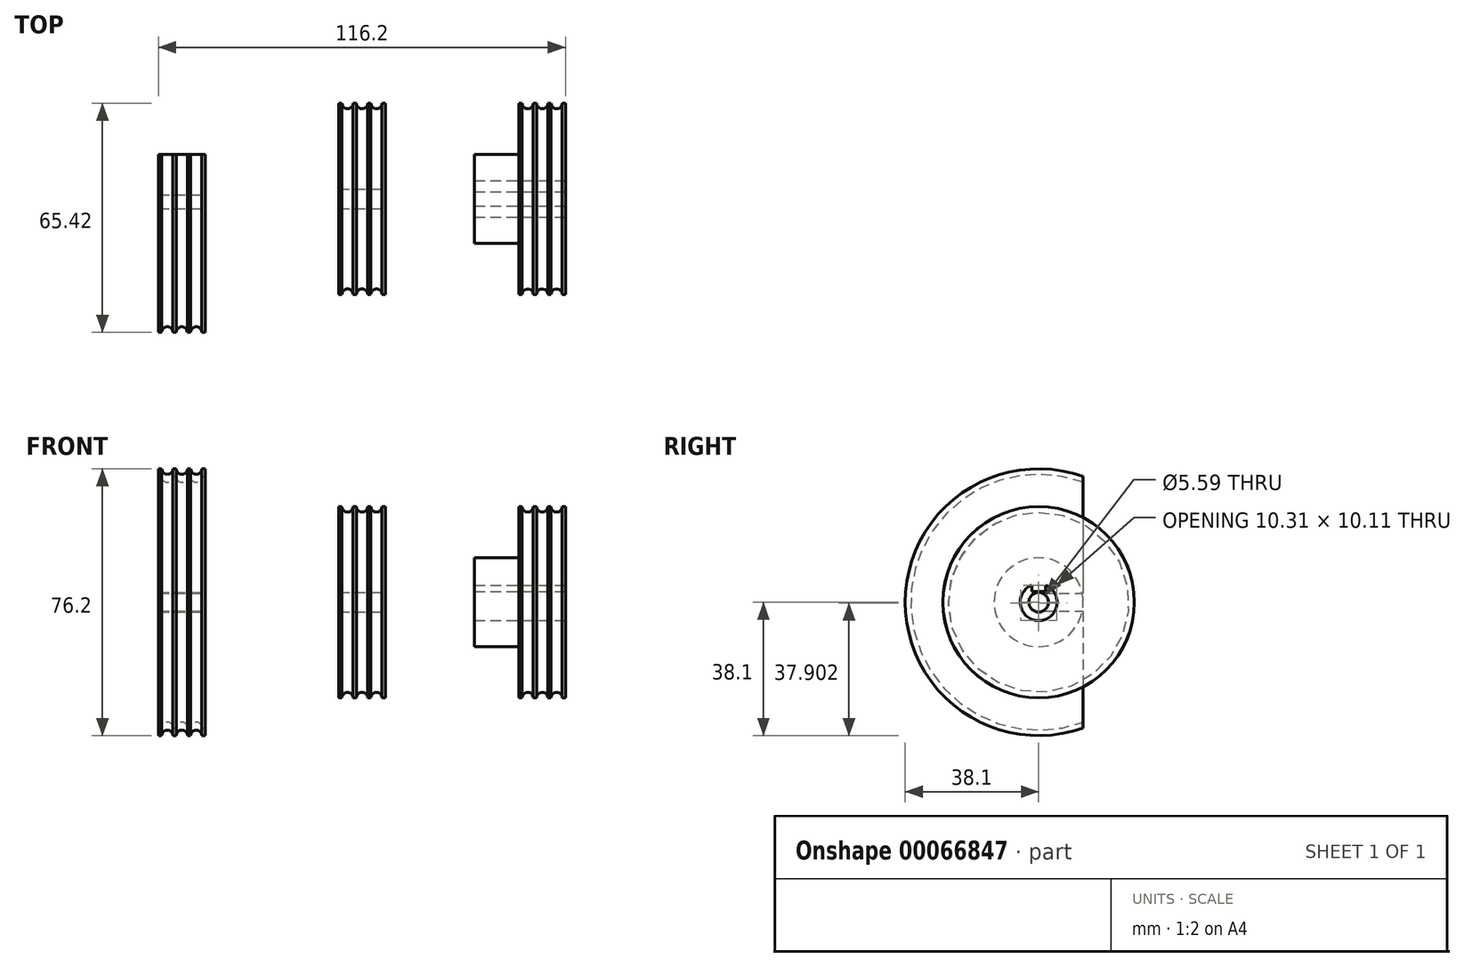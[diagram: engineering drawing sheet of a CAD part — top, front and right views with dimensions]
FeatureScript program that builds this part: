
annotation { "Feature Type Name" : "Feature", "Feature Type Description" : "" }
export const myFeature = defineFeature(function(context is Context, id is Id, definition is map)
    precondition{}
    {
        {
            var Q0;
            Q0=qCreatedBy(makeId("Front.planeOp"),FACE);
            var sketch = newSketch(context, id + "F0", { "sketchPlane" : qUnion([Q0])});
            skArc(sketch, "E0", {"start": v(-12.38, 27.32) * mm, "mid": v(-10.8, 25.72) * mm, "end": v(-9.2, 27.3) * mm});
            skArc(sketch, "E1", {"start": v(-8.25, 27.3) * mm, "mid": v(-6.67, 25.72) * mm, "end": v(-5.08, 27.3) * mm});
            skArc(sketch, "E2", {"start": v(-4.13, 27.3) * mm, "mid": v(-2.54, 25.72) * mm, "end": v(-0.95, 27.3) * mm});
            skLineSegment(sketch, "E3", {"start": v(-9.2, 27.3) * mm, "end": v(-8.25, 27.3) * mm});
            skLineSegment(sketch, "E4", {"start": v(-12.38, 27.32) * mm, "end": v(-13.33, 27.32) * mm});
            skLineSegment(sketch, "E5", {"start": v(-0.95, 27.3) * mm, "end": v(0, 27.3) * mm});
            skLineSegment(sketch, "E6", {"start": v(-5.08, 27.3) * mm, "end": v(-4.13, 27.3) * mm});
            skLineSegment(sketch, "E7", {"start": v(-13.33, 27.32) * mm, "end": v(-13.33, 0) * mm});
            skLineSegment(sketch, "E8", {"start": v(-13.33, 0) * mm, "end": v(0, 0) * mm});
            skLineSegment(sketch, "E9", {"start": v(0, 0) * mm, "end": v(0, 27.3) * mm});
            skArc(sketch, "E10", {"start": v(39.05, 27.32) * mm, "mid": v(40.63, 25.72) * mm, "end": v(42.23, 27.3) * mm});
            skArc(sketch, "E11", {"start": v(43.18, 27.3) * mm, "mid": v(44.77, 25.72) * mm, "end": v(46.35, 27.3) * mm});
            skArc(sketch, "E12", {"start": v(47.3, 27.3) * mm, "mid": v(48.9, 25.72) * mm, "end": v(50.48, 27.3) * mm});
            skLineSegment(sketch, "E13", {"start": v(42.23, 27.3) * mm, "end": v(43.18, 27.3) * mm});
            skLineSegment(sketch, "E14", {"start": v(39.05, 27.32) * mm, "end": v(38.1, 27.32) * mm});
            skLineSegment(sketch, "E15", {"start": v(50.48, 27.3) * mm, "end": v(51.43, 27.3) * mm});
            skLineSegment(sketch, "E16", {"start": v(46.35, 27.3) * mm, "end": v(47.3, 27.3) * mm});
            skLineSegment(sketch, "E17", {"start": v(38.1, 27.32) * mm, "end": v(38.1, 0) * mm});
            skLineSegment(sketch, "E18", {"start": v(38.1, 0) * mm, "end": v(51.43, 0) * mm});
            skLineSegment(sketch, "E19", {"start": v(51.43, 0) * mm, "end": v(51.43, 27.3) * mm});
            skArc(sketch, "E20", {"start": v(-59.69, 38.1) * mm, "mid": v(-58.1, 36.51) * mm, "end": v(-56.51, 38.1) * mm});
            skArc(sketch, "E21", {"start": v(-55.56, 38.1) * mm, "mid": v(-53.97, 36.51) * mm, "end": v(-52.39, 38.1) * mm});
            skLineSegment(sketch, "E22", {"start": v(-60.64, 38.1) * mm, "end": v(-59.69, 38.1) * mm});
            skLineSegment(sketch, "E23", {"start": v(-63.82, 38.1) * mm, "end": v(-64.77, 38.1) * mm});
            skLineSegment(sketch, "E24", {"start": v(-52.39, 38.1) * mm, "end": v(-51.43, 38.1) * mm});
            skLineSegment(sketch, "E25", {"start": v(-56.51, 38.1) * mm, "end": v(-55.56, 38.1) * mm});
            skLineSegment(sketch, "E26", {"start": v(-64.77, 38.1) * mm, "end": v(-64.77, 0) * mm});
            skLineSegment(sketch, "E27", {"start": v(-64.77, 0) * mm, "end": v(-51.43, 0) * mm});
            skLineSegment(sketch, "E28", {"start": v(-51.43, 0) * mm, "end": v(-51.43, 38.1) * mm});
            skArc(sketch, "E29", {"start": v(-63.82, 38.1) * mm, "mid": v(-62.23, 36.51) * mm, "end": v(-60.64, 38.1) * mm});
            skSolve(sketch);
        }
        {
            var Q0;
            Q0=makeQuery(id+"F0.imprint","IMPRINT",FACE,{"disambiguationData":[TD([[makeQuery(id+"F0.imprint","IMPRINT",EDGE,{"derivedFrom":sQuery(id+"F0.wireOp",EDGE,"E0")}),-1.0]])]});
            var Q1;
            Q1=makeQuery(id+"F0.imprint","IMPRINT",FACE,{"disambiguationData":[TD([[makeQuery(id+"F0.imprint","IMPRINT",EDGE,{"derivedFrom":sQuery(id+"F0.wireOp",EDGE,"E10")}),-1.0]])]});
            var Q2;
            Q2=makeQuery(id+"F0.imprint","IMPRINT",FACE,{"disambiguationData":[TD([[makeQuery(id+"F0.imprint","IMPRINT",EDGE,{"derivedFrom":sQuery(id+"F0.wireOp",EDGE,"d0020f9b-7314-46ad-96e7-04e3143bfc31")}),-1.0]])]});
            var Q3;
            Q3=makeQuery(id+"F0.imprint","IMPRINT",FACE,{"disambiguationData":[TD([[makeQuery(id+"F0.imprint","IMPRINT",EDGE,{"derivedFrom":sQuery(id+"F0.wireOp",EDGE,"E20")}),-1.0]])]});
            var Q4;
            Q4=sQuery(id+"F0.wireOp",EDGE,"E8");
            revolve(context, id + "F1", {"entities" : qUnion([Q0, Q1, Q2, Q3]), "axis" : qUnion([Q4]), "revolveType" : RevolveType.FULL});
        }
        {
            var Q0;
            Q0=makeQuery(id+"F1.opRevolve","SWEPT_FACE",FACE,{"disambiguationData":[OSD([sQuery(id+"F0.wireOp",EDGE,"E9")])]});
            var sketch = newSketch(context, id + "F2", { "sketchPlane" : qUnion([Q0])});
            skCircle(sketch, "E30.cCircle", {"center": v(0, 0) * mm, "radius": 6.6 * mm, "construction": true});
            skLineSegment(sketch, "E30.0", {"start": v(3.81, 6.6) * mm, "end": v(7.63, 0) * mm, "construction": true});
            skLineSegment(sketch, "E30.1", {"start": v(7.63, 0) * mm, "end": v(3.81, -6.6) * mm, "construction": true});
            skLineSegment(sketch, "E30.2", {"start": v(3.81, -6.6) * mm, "end": v(-3.81, -6.6) * mm, "construction": true});
            skLineSegment(sketch, "E30.3", {"start": v(-3.81, -6.6) * mm, "end": v(-7.63, 0) * mm, "construction": true});
            skLineSegment(sketch, "E30.4", {"start": v(-7.63, 0) * mm, "end": v(-3.81, 6.6) * mm, "construction": true});
            skLineSegment(sketch, "E30.5", {"start": v(-3.81, 6.6) * mm, "end": v(3.81, 6.6) * mm, "construction": true});
            skPoint(sketch, "E30.0.midPoint", {"position": v(5.72, 3.3) * mm});
            skCircle(sketch, "E31", {"center": v(0, 0) * mm, "radius": 2.8 * mm});
            skSolve(sketch);
        }
        {
            var Q0;
            Q0 = qSketchRegion(id + "F2", true);
            extrude(context, id + "F3", {"entities" : qUnion([Q0]), "operationType" : NewBodyOperationType.REMOVE, "endBound" : BoundingType.THROUGH_ALL, "oppositeDirection" : true, "depth" : 25.4 * mm});
        }
        {
            var Q0;
            Q0=makeQuery(id+"F1.opRevolve","SWEPT_FACE",FACE,{"disambiguationData":[OSD([sQuery(id+"F0.wireOp",EDGE,"E19")])]});
            var sketch = newSketch(context, id + "F4", { "sketchPlane" : qUnion([Q0])});
            skArc(sketch, "E32", {"start": v(-2, 4.86) * mm, "mid": v(0, -5.25) * mm, "end": v(2, 4.86) * mm});
            skLineSegment(sketch, "E33.top", {"start": v(-2, 3) * mm, "end": v(2, 3) * mm});
            skLineSegment(sketch, "E33.left", {"start": v(-2, 5) * mm, "end": v(-2, 3) * mm});
            skLineSegment(sketch, "E33.right", {"start": v(2, 5) * mm, "end": v(2, 3) * mm});
            skSolve(sketch);
        }
        {
            var Q0;
            {var subQ0=sQuery(id+"F4.wireOp",EDGE,"E32");Q0=makeQuery(id+"F4.imprint","IMPRINT",FACE,{"disambiguationData":[TD([[makeQuery(id+"F4.imprint","IMPRINT",EDGE,{"derivedFrom":subQ0}),1.0]])]});}
            extrude(context, id + "F5", {"entities" : qUnion([Q0]), "operationType" : NewBodyOperationType.REMOVE, "oppositeDirection" : true, "depth" : 25.4 * mm});
        }
        {
            var Q0;
            Q0=makeQuery(id+"F1.opRevolve","SWEPT_FACE",FACE,{"disambiguationData":[OSD([sQuery(id+"F0.wireOp",EDGE,"E17")])]});
            var sketch = newSketch(context, id + "F6", { "sketchPlane" : qUnion([Q0])});
            skCircle(sketch, "E34", {"center": v(0, 0) * mm, "radius": 12.7 * mm});
            skSolve(sketch);
        }
        {
            var Q0;
            Q0=makeQuery(id+"F6.imprint","IMPRINT",FACE,{"disambiguationData":[TD([[makeQuery(id+"F6.imprint","IMPRINT",EDGE,{"derivedFrom":sQuery(id+"F6.wireOp",EDGE,"E34")}),1.0]])]});
            var Q1;
            Q1=sQuery(id+"F6.wireOp",EDGE,"E34");
            extrude(context, id + "F7", {"entities" : qUnion([Q0]), "operationType" : NewBodyOperationType.ADD, "surfaceEntities" : qUnion([Q1]), "depth" : 12.7 * mm});
        }
        {
            var Q0;
            Q0=makeQuery(id+"F1.opRevolve","SWEPT_FACE",FACE,{"disambiguationData":[OSD([sQuery(id+"F0.wireOp",EDGE,"E28")])]});
            var sketch = newSketch(context, id + "F8", { "sketchPlane" : qUnion([Q0])});
            skCircle(sketch, "E35", {"center": v(0, 0) * mm, "radius": 2.54 * mm});
            skLineSegment(sketch, "E36", {"start": v(12.7, 35.92) * mm, "end": v(12.7, -35.92) * mm});
            skLineSegment(sketch, "E37", {"start": v(0, 2.54) * mm, "end": v(12.7, 2.54) * mm});
            skLineSegment(sketch, "E38", {"start": v(0, -2.54) * mm, "end": v(12.7, -2.54) * mm});
            skSolve(sketch);
        }
        {
            var Q0;
            {var subQ0=sQuery(id+"F8.wireOp",EDGE,"E36");Q0=makeQuery(id+"F8.imprint","IMPRINT",FACE,{"disambiguationData":[TD([[makeQuery(id+"F8.imprint","IMPRINT",EDGE,{"derivedFrom":subQ0}),1.0]])]});}
            extrude(context, id + "F9", {"entities" : qUnion([Q0]), "operationType" : NewBodyOperationType.REMOVE, "endBound" : BoundingType.THROUGH_ALL, "oppositeDirection" : true, "depth" : 25.4 * mm});
        }
        {
            var Q0;
            Q0 = qSketchRegion(id + "F8", true);
            var Q1;
            Q1=sQuery(id+"F8.wireOp",EDGE,"E35");
            extrude(context, id + "F10", {"entities" : qUnion([Q0]), "operationType" : NewBodyOperationType.REMOVE, "surfaceEntities" : qUnion([Q1]), "oppositeDirection" : true, "depth" : 25.4 * mm});
        }
    });
